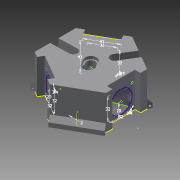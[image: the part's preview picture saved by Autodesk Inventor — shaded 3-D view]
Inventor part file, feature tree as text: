
AUTODESK INVENTOR PART (.ipt)
format: ipt  version: 2015 SP1 (Build 190203100, 203)  size: 780,800 bytes
history: native  units: mm
features: sketch x17, extrude x11, fillet x3, hole x3, loft x2, other x2, plane x1, pattern_circular x1, chamfer x1
ambient origin geometry x8: Origin, YZ Plane, XZ Plane, XY Plane, X Axis, Y Axis, Z Axis, Center Point
bodies: Body1 (feature_tree)
feature tree (41):
  extrude  "Extrusion2"  Depth=41.0mm
  extrude  "Extrusion3"  Depth=26.0mm
  extrude  "Extrusion4"  Depth=12.3mm
  extrude  "Extrusion5"  Depth=13.0mm TaperAngle=0.0deg
  sketch  "Sketch5"  dims[d16=4.0mm d17=0.0mm d18=3.0mm d19=0.0mm d20=41.0mm]
  extrude  "Extrusion6"  Depth=4.0mm TaperAngle=0.0deg
  fillet  "Fillet1"  Radius=41.0mm
  extrude  "Extrusion7"  Depth=32.0mm
  sketch  "Sketch6"  dims[d21=41.0mm d22=32.0mm]
  plane  "Work Plane1"
  extrude  "Extrusion8"  Depth=3.4mm
  fillet  "Fillet2"  Radius=3.0mm
  sketch  "Sketch8"  dims[d29=3.0mm d30=-0.698132mm d31=4.0mm]
  sketch  "Sketch9"  dims[d32=12.0mm d33=0.0mm d34=26.0mm d35=0.0mm]
  sketch  "Sketch10"  dims[d36=4.0mm d39=32.0mm d40=32.0mm d41=3.4mm d42=3.0mm]
  loft  "Loft2"
  other  "Work Point1"
  other  "Work Point2"
  loft  "Loft3"
  extrude  "Extrusion9"  Depth=4.0mm
  extrude  "Extrusion10"  Depth=32.0mm
  extrude  "Extrusion11"  TaperAngle=0.0deg  [1 undecoded]
  hole  "Hole1"  [1 undecoded]
  pattern_circular  "Circular Pattern1"  Count=2  [1 undecoded]
  hole  "Hole2"  [1 undecoded]
  hole  "Hole3"  [1 undecoded]
  chamfer  "Chamfer1"  Distance=8.0mm
  extrude  "Extrusion12"  Depth=4.0mm
  fillet  "Fillet3"  Radius=6.0mm
  sketch  "Sketch1"  dims[d0=60.0mm d3=41.0mm]
  sketch  "Sketch2"  dims[d8=16.0mm d9=26.0mm]
  sketch  "Sketch3"  dims[d10=37.0mm d11=0.0mm d12=12.3mm]
  sketch  "Sketch4"  dims[d13=16.3mm d14=13.0mm d15=0.0mm]
  sketch  "Sketch7"  dims[d23=32.0mm d24=3.4mm d28=3.0mm]
  sketch  "3D Sketch3"
  sketch  "3D Sketch4"
  sketch  "Sketch12"  dims[d43=2.0mm d46=32.0mm d47=32.0mm d48=3.4mm d49=3.0mm]
  sketch  "Sketch13"  dims[d56=0.0mm d57=90.0deg d58=0.0mm d59=90.0deg]
  sketch  "Sketch14"  dims[d60=0.0mm d61=90.0deg d62=0.0mm d63=90.0deg]
  sketch  "Sketch15"  dims[d64=0.0mm d65=90.0deg]
  sketch  "Sketch17"  dims[d66=0.0mm d67=90.0deg d68=20.0mm d69=20.0mm d70=8.0mm d71=0.0mm d72=8.0mm d73=0.0mm d74=6.0mm d75=6.0mm d76=0.0mm d77=30.0mm d78=360.0deg d80=3.0mm d81=6.0mm d82=4.0mm d83=2.0mm d84=90.0deg d85=8.0mm d86=20.594885mm d87=3.0mm d88=6.0mm d89=4.0mm d90=2.0mm d91=90.0deg d92=8.0mm d93=20.594885mm d94=3.0mm d95=6.0mm d96=4.0mm d97=2.0mm d98=90.0deg d99=8.0mm d100=20.594885mm d101=6.0mm d102=2.0mm d103=45.0deg d104=6.0mm d105=0.0mm d106=4.0mm]
note: 5 required parameter values undecoded (feature->parameter linkage not recoverable at this tier; creation-order binding heuristic only, values carry confidence <= 0.55)
